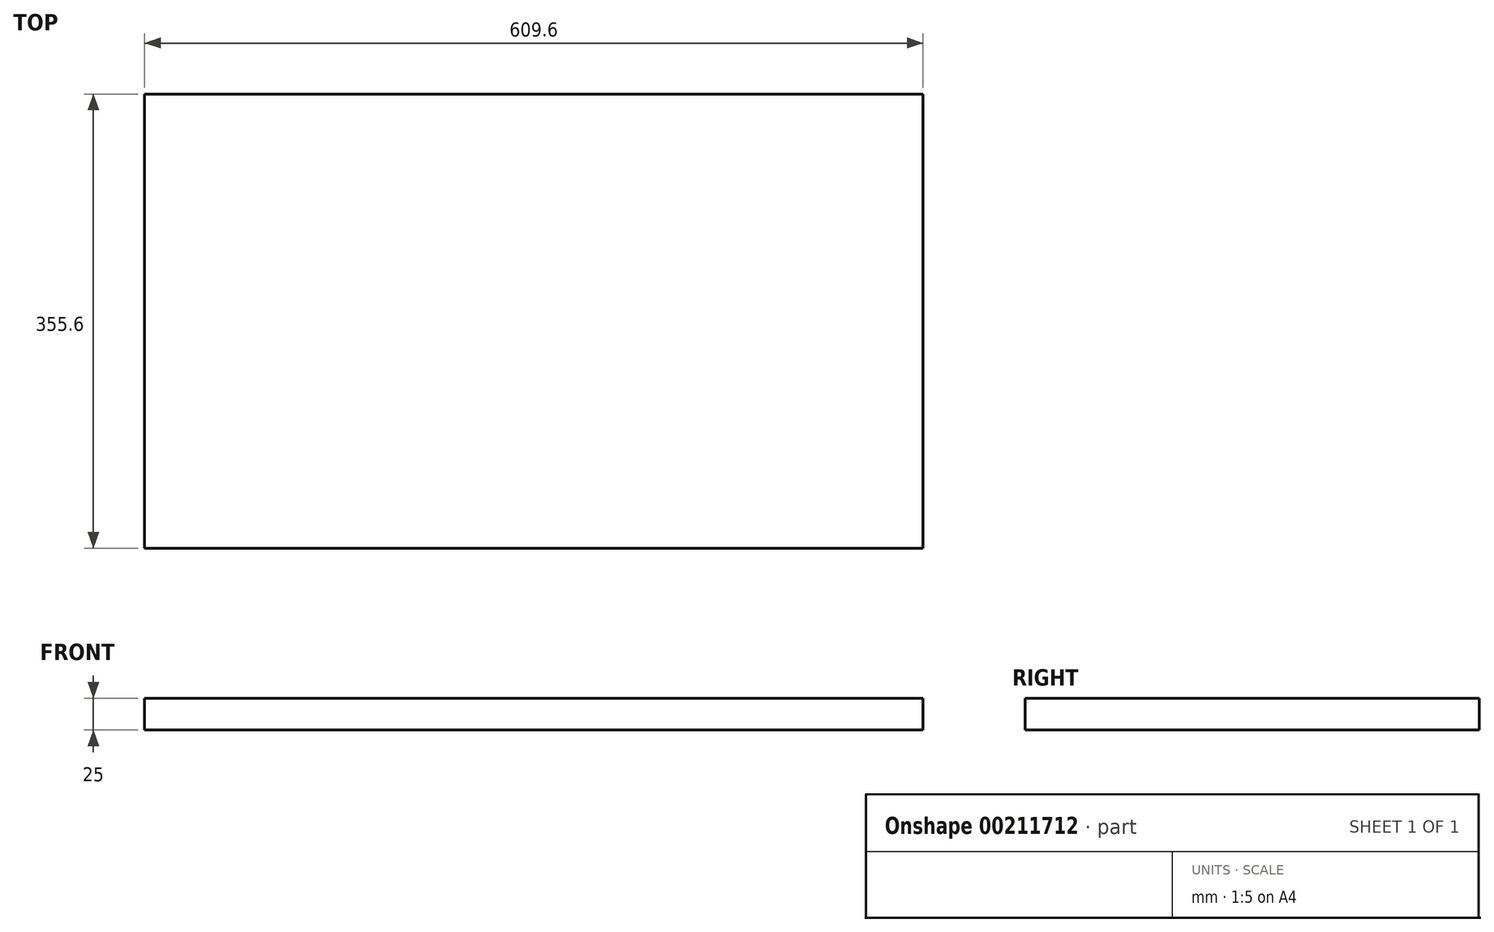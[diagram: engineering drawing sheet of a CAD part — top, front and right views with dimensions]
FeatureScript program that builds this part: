
annotation { "Feature Type Name" : "Feature", "Feature Type Description" : "" }
export const myFeature = defineFeature(function(context is Context, id is Id, definition is map)
    precondition{}
    {
        {
            var Q0;
            Q0=qCreatedBy(makeId("Top.planeOp"),FACE);
            var sketch = newSketch(context, id + "F1", { "sketchPlane" : qUnion([Q0])});
            skLineSegment(sketch, "E0.bottom", {"start": v(304.8, 177.8) * mm, "end": v(-304.8, 177.8) * mm});
            skLineSegment(sketch, "E0.top", {"start": v(304.8, -177.8) * mm, "end": v(-304.8, -177.8) * mm});
            skLineSegment(sketch, "E0.left", {"start": v(304.8, 177.8) * mm, "end": v(304.8, -177.8) * mm});
            skLineSegment(sketch, "E0.right", {"start": v(-304.8, 177.8) * mm, "end": v(-304.8, -177.8) * mm});
            skPoint(sketch, "E0.middle", {"position": v(0, 0) * mm});
            skSolve(sketch);
        }
        {
            var Q0;
            Q0=makeQuery(id+"F1.imprint","IMPRINT",FACE,{"disambiguationData":[TD([[makeQuery(id+"F1.imprint","IMPRINT",EDGE,{"derivedFrom":sQuery(id+"F1.wireOp",EDGE,"E0.bottom")}),1.0]])]});
            extrude(context, id + "F0", {"entities" : qUnion([Q0]), "oppositeDirection" : true, "depth" : 25 * mm});
        }
    });
